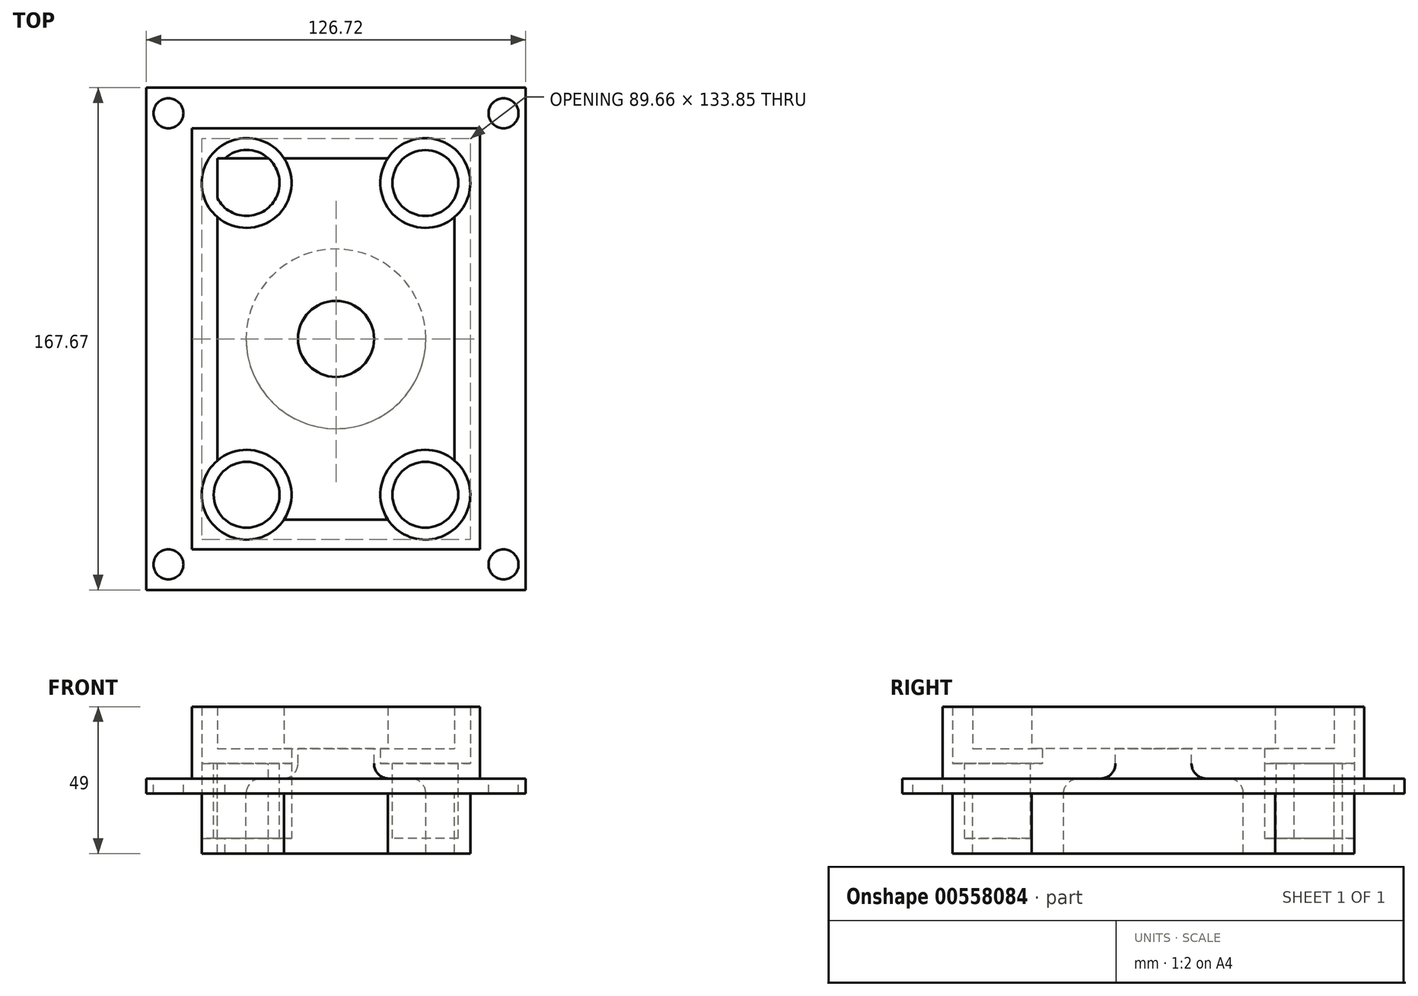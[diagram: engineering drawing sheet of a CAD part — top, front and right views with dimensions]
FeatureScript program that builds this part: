
annotation { "Feature Type Name" : "Feature", "Feature Type Description" : "" }
export const myFeature = defineFeature(function(context is Context, id is Id, definition is map)
    precondition{}
    {
        {
            var Q0;
            Q0=qCreatedBy(makeId("Top.planeOp"),FACE);
            var sketch = newSketch(context, id + "F0", { "sketchPlane" : qUnion([Q0])});
            skLineSegment(sketch, "E0.bottom", {"start": v(-50.77, 68.15) * mm, "end": v(45.43, 68.15) * mm});
            skLineSegment(sketch, "E0.top", {"start": v(-50.77, -72.5) * mm, "end": v(45.43, -72.5) * mm});
            skLineSegment(sketch, "E0.left", {"start": v(-50.77, 68.15) * mm, "end": v(-50.77, -72.5) * mm});
            skLineSegment(sketch, "E0.right", {"start": v(45.43, 68.15) * mm, "end": v(45.43, -72.5) * mm});
            skCircle(sketch, "E1", {"center": v(-2.67, -2.17) * mm, "radius": 12.7 * mm});
            skLineSegment(sketch, "E2.bottom", {"start": v(-42.27, 58.15) * mm, "end": v(36.93, 58.15) * mm});
            skLineSegment(sketch, "E2.top", {"start": v(-42.27, -62.5) * mm, "end": v(36.93, -62.5) * mm});
            skLineSegment(sketch, "E2.left", {"start": v(-42.27, 58.15) * mm, "end": v(-42.27, -62.5) * mm});
            skLineSegment(sketch, "E2.right", {"start": v(36.93, 58.15) * mm, "end": v(36.93, -62.5) * mm});
            skCircle(sketch, "E3", {"center": v(-32.5, 49.88) * mm, "radius": 15 * mm});
            skCircle(sketch, "E4", {"center": v(-32.5, -54.23) * mm, "radius": 15 * mm});
            skCircle(sketch, "E5", {"center": v(27.17, -54.23) * mm, "radius": 15 * mm});
            skLineSegment(sketch, "E6.bottom", {"start": v(-32.5, 49.88) * mm, "end": v(27.17, 49.88) * mm, "construction": true});
            skLineSegment(sketch, "E6.top", {"start": v(-32.5, -54.23) * mm, "end": v(27.17, -54.23) * mm, "construction": true});
            skLineSegment(sketch, "E6.left", {"start": v(-32.5, 49.88) * mm, "end": v(-32.5, -54.23) * mm, "construction": true});
            skLineSegment(sketch, "E6.right", {"start": v(27.17, 49.88) * mm, "end": v(27.17, -54.23) * mm, "construction": true});
            skCircle(sketch, "E7", {"center": v(27.17, 49.88) * mm, "radius": 15 * mm});
            skCircle(sketch, "E8", {"center": v(-32.5, 49.88) * mm, "radius": 11 * mm});
            skCircle(sketch, "E9", {"center": v(27.17, 49.88) * mm, "radius": 11 * mm});
            skCircle(sketch, "E10", {"center": v(27.17, -54.23) * mm, "radius": 11 * mm});
            skCircle(sketch, "E11", {"center": v(-32.5, -54.23) * mm, "radius": 11 * mm});
            skSolve(sketch);
        }
        {
            var Q0;
            Q0=makeQuery(id+"F0.imprint","IMPRINT",FACE,{"disambiguationData":[TD([[makeQuery(id+"F0.imprint","IMPRINT",EDGE,{"derivedFrom":sQuery(id+"F0.wireOp",EDGE,"E1")}),-1.0]])]});
            var Q1;
            Q1=makeQuery(id+"F0.imprint","IMPRINT",FACE,{"disambiguationData":[TD([[makeQuery(id+"F0.imprint","IMPRINT",EDGE,{"derivedFrom":sQuery(id+"F0.wireOp",EDGE,"E3")}),1.0]])]});
            var Q2;
            Q2=makeQuery(id+"F0.imprint","IMPRINT",FACE,{"disambiguationData":[TD([[makeQuery(id+"F0.imprint","IMPRINT",EDGE,{"derivedFrom":sQuery(id+"F0.wireOp",EDGE,"E7")}),1.0]])]});
            var Q3;
            Q3=makeQuery(id+"F0.imprint","IMPRINT",FACE,{"disambiguationData":[TD([[makeQuery(id+"F0.imprint","IMPRINT",EDGE,{"derivedFrom":sQuery(id+"F0.wireOp",EDGE,"E4")}),1.0]])]});
            var Q4;
            Q4=makeQuery(id+"F0.imprint","IMPRINT",FACE,{"disambiguationData":[TD([[makeQuery(id+"F0.imprint","IMPRINT",EDGE,{"derivedFrom":sQuery(id+"F0.wireOp",EDGE,"E0.bottom")}),-1.0]])]});
            var Q5;
            Q5=makeQuery(id+"F0.imprint","IMPRINT",FACE,{"disambiguationData":[TD([[makeQuery(id+"F0.imprint","IMPRINT",EDGE,{"derivedFrom":sQuery(id+"F0.wireOp",EDGE,"E5")}),1.0]])]});
            var Q6;
            {var subQ0=sQuery(id+"F0.wireOp",EDGE,"E2.left");var subQ1=sQuery(id+"F0.wireOp",EDGE,"E2.top");var subQ2=makeQuery(id+"F0.imprint","INTERSECT",VERTEX,{"derivedFrom":[subQ1,subQ0]});Q6=makeQuery(id+"F0.imprint","IMPRINT",FACE,{"disambiguationData":[TD([[makeQuery(id+"F0.imprint","IMPRINT",EDGE,{"disambiguationData":[TD([[subQ2,-1.0]])],"derivedFrom":subQ1}),-1.0]])]});}
            var Q7;
            {var subQ1=sQuery(id+"F0.wireOp",EDGE,"E2.top");var subQ5=sQuery(id+"F0.wireOp",EDGE,"E5");var subQ9=makeQuery(id+"F0.imprint","INTERSECT",VERTEX,{"derivedFrom":[subQ1,subQ5]});Q7=makeQuery(id+"F0.imprint","IMPRINT",FACE,{"disambiguationData":[TD([[makeQuery(id+"F0.imprint","IMPRINT",EDGE,{"disambiguationData":[TD([[subQ9,-1.0]])],"derivedFrom":subQ1}),-1.0]])]});}
            var Q8;
            {var subQ3=sQuery(id+"F0.wireOp",EDGE,"E7");var subQ5=sQuery(id+"F0.wireOp",EDGE,"E2.bottom");var subQ9=makeQuery(id+"F0.imprint","INTERSECT",VERTEX,{"derivedFrom":[subQ5,subQ3]});Q8=makeQuery(id+"F0.imprint","IMPRINT",FACE,{"disambiguationData":[TD([[makeQuery(id+"F0.imprint","IMPRINT",EDGE,{"disambiguationData":[TD([[subQ9,-1.0]])],"derivedFrom":subQ5}),1.0]])]});}
            var Q9;
            {var subQ0=sQuery(id+"F0.wireOp",EDGE,"E2.right");var subQ1=sQuery(id+"F0.wireOp",EDGE,"E2.bottom");var subQ2=makeQuery(id+"F0.imprint","INTERSECT",VERTEX,{"derivedFrom":[subQ1,subQ0]});Q9=makeQuery(id+"F0.imprint","IMPRINT",FACE,{"disambiguationData":[TD([[makeQuery(id+"F0.imprint","IMPRINT",EDGE,{"disambiguationData":[TD([[subQ2,1.0]])],"derivedFrom":subQ1}),-1.0]])]});}
            var Q10;
            {var subQ1=sQuery(id+"F0.wireOp",EDGE,"E2.left");var subQ6=sQuery(id+"F0.wireOp",EDGE,"E2.bottom");var subQ7=makeQuery(id+"F0.imprint","INTERSECT",VERTEX,{"derivedFrom":[subQ6,subQ1]});Q10=makeQuery(id+"F0.imprint","IMPRINT",FACE,{"disambiguationData":[TD([[makeQuery(id+"F0.imprint","IMPRINT",EDGE,{"disambiguationData":[TD([[subQ7,-1.0]])],"derivedFrom":subQ6}),1.0]])]});}
            var Q11;
            {var subQ0=sQuery(id+"F0.wireOp",EDGE,"E2.left");var subQ1=sQuery(id+"F0.wireOp",EDGE,"E2.bottom");var subQ2=makeQuery(id+"F0.imprint","INTERSECT",VERTEX,{"derivedFrom":[subQ1,subQ0]});Q11=makeQuery(id+"F0.imprint","IMPRINT",FACE,{"disambiguationData":[TD([[makeQuery(id+"F0.imprint","IMPRINT",EDGE,{"disambiguationData":[TD([[subQ2,-1.0]])],"derivedFrom":subQ1}),-1.0]])]});}
            var Q12;
            {var subQ0=sQuery(id+"F0.wireOp",EDGE,"E2.right");var subQ1=sQuery(id+"F0.wireOp",EDGE,"E2.top");var subQ2=makeQuery(id+"F0.imprint","INTERSECT",VERTEX,{"derivedFrom":[subQ1,subQ0]});Q12=makeQuery(id+"F0.imprint","IMPRINT",FACE,{"disambiguationData":[TD([[makeQuery(id+"F0.imprint","IMPRINT",EDGE,{"disambiguationData":[TD([[subQ2,1.0]])],"derivedFrom":subQ1}),1.0]])]});}
            var Q13;
            {var subQ0=sQuery(id+"F0.wireOp",EDGE,"E2.left");var subQ1=sQuery(id+"F0.wireOp",EDGE,"E2.top");var subQ2=makeQuery(id+"F0.imprint","INTERSECT",VERTEX,{"derivedFrom":[subQ1,subQ0]});Q13=makeQuery(id+"F0.imprint","IMPRINT",FACE,{"disambiguationData":[TD([[makeQuery(id+"F0.imprint","IMPRINT",EDGE,{"disambiguationData":[TD([[subQ2,-1.0]])],"derivedFrom":subQ1}),1.0]])]});}
            extrude(context, id + "F1", {"entities" : qUnion([Q0, Q1, Q2, Q3, Q4, Q5, Q6, Q7, Q8, Q9, Q10, Q11, Q12, Q13]), "oppositeDirection" : true, "depth" : 5 * mm, "offsetDistance" : 25 * mm});
        }
        {
            var Q0;
            Q0=makeQuery(id+"F0.imprint","IMPRINT",FACE,{"disambiguationData":[TD([[makeQuery(id+"F0.imprint","IMPRINT",EDGE,{"derivedFrom":sQuery(id+"F0.wireOp",EDGE,"E1")}),-1.0]])]});
            extrude(context, id + "F2", {"entities" : qUnion([Q0]), "operationType" : NewBodyOperationType.ADD, "depth" : 5 * mm, "offsetDistance" : 25 * mm});
        }
        {
            var Q0;
            Q0=makeQuery(id+"F0.imprint","IMPRINT",FACE,{"disambiguationData":[TD([[makeQuery(id+"F0.imprint","IMPRINT",EDGE,{"derivedFrom":sQuery(id+"F0.wireOp",EDGE,"E0.bottom")}),-1.0]])]});
            extrude(context, id + "F3", {"entities" : qUnion([Q0]), "operationType" : NewBodyOperationType.ADD, "depth" : 19 * mm, "offsetDistance" : 25 * mm});
        }
        {
            var Q0;
            Q0=makeQuery(id+"F1.opExtrude","CAP_FACE",FACE,{"disambiguationData":[OSD([sQuery(id+"F0.wireOp",EDGE,"E0.bottom"),sQuery(id+"F0.wireOp",EDGE,"E0.top"),sQuery(id+"F0.wireOp",EDGE,"E0.left"),sQuery(id+"F0.wireOp",EDGE,"E0.right"),sQuery(id+"F0.wireOp",EDGE,"E1")])],"isStart":false});
            var sketch = newSketch(context, id + "F4", { "sketchPlane" : qUnion([Q0])});
            skLineSegment(sketch, "E12.bottom", {"start": v(-66.03, 86.01) * mm, "end": v(60.7, 86.01) * mm});
            skLineSegment(sketch, "E12.top", {"start": v(-66.03, -81.66) * mm, "end": v(60.7, -81.66) * mm});
            skLineSegment(sketch, "E12.left", {"start": v(-66.03, 86.01) * mm, "end": v(-66.03, -81.66) * mm});
            skLineSegment(sketch, "E12.right", {"start": v(60.7, 86.01) * mm, "end": v(60.7, -81.66) * mm});
            skPoint(sketch, "E12.middle", {"position": v(-2.67, 2.17) * mm});
            skLineSegment(sketch, "E13.bottom", {"start": v(-58.6, 77.5) * mm, "end": v(53.27, 77.5) * mm, "construction": true});
            skLineSegment(sketch, "E13.top", {"start": v(-58.6, -73.15) * mm, "end": v(53.27, -73.15) * mm, "construction": true});
            skLineSegment(sketch, "E13.left", {"start": v(-58.6, 77.5) * mm, "end": v(-58.6, -73.15) * mm, "construction": true});
            skLineSegment(sketch, "E13.right", {"start": v(53.27, 77.5) * mm, "end": v(53.27, -73.15) * mm, "construction": true});
            skCircle(sketch, "E14", {"center": v(-58.6, 77.5) * mm, "radius": 5 * mm});
            skCircle(sketch, "E15", {"center": v(53.27, 77.5) * mm, "radius": 5 * mm});
            skCircle(sketch, "E16", {"center": v(53.27, -73.15) * mm, "radius": 5 * mm});
            skCircle(sketch, "E17", {"center": v(-58.6, -73.15) * mm, "radius": 5 * mm});
            skCircle(sketch, "E18", {"center": v(-2.67, 2.17) * mm, "radius": 30 * mm});
            skSolve(sketch);
        }
        {
            var Q0;
            Q0=makeQuery(id+"F4.imprint","IMPRINT",FACE,{"disambiguationData":[TD([[makeQuery(id+"F4.imprint","IMPRINT",EDGE,{"derivedFrom":sQuery(id+"F4.wireOp",EDGE,"E12.bottom")}),-1.0]])]});
            var Q1;
            Q1=makeQuery(id+"F4.imprint","IMPRINT",FACE,{"disambiguationData":[TD([[makeQuery(id+"F4.imprint","IMPRINT",EDGE,{"derivedFrom":makeQuery(id+"F1.opExtrude","CAP_EDGE",EDGE,{"disambiguationData":[OSD([sQuery(id+"F0.wireOp",EDGE,"E0.bottom")])],"isStart":false})}),1.0]])]});
            var Q2;
            Q2=makeQuery(id+"F2.opExtrude","CAP_FACE",FACE,{"disambiguationData":[OSD([sQuery(id+"F0.wireOp",EDGE,"E1"),sQuery(id+"F0.wireOp",EDGE,"E2.bottom"),sQuery(id+"F0.wireOp",EDGE,"E2.top"),sQuery(id+"F0.wireOp",EDGE,"E2.left"),sQuery(id+"F0.wireOp",EDGE,"E2.right"),sQuery(id+"F0.wireOp",EDGE,"E3"),sQuery(id+"F0.wireOp",EDGE,"E4"),sQuery(id+"F0.wireOp",EDGE,"E5"),sQuery(id+"F0.wireOp",EDGE,"E7")])],"isStart":false});
            var Q3;
            Q3=makeQuery(id+"F4.imprint","IMPRINT",FACE,{"disambiguationData":[TD([[makeQuery(id+"F4.imprint","IMPRINT",EDGE,{"derivedFrom":makeQuery(id+"F1.opExtrude","CAP_EDGE",EDGE,{"disambiguationData":[OSD([sQuery(id+"F0.wireOp",EDGE,"E10")])],"isStart":false})}),-1.0]])]});
            var Q4;
            Q4=makeQuery(id+"F4.imprint","IMPRINT",FACE,{"disambiguationData":[TD([[makeQuery(id+"F4.imprint","IMPRINT",EDGE,{"derivedFrom":makeQuery(id+"F1.opExtrude","CAP_EDGE",EDGE,{"disambiguationData":[OSD([sQuery(id+"F0.wireOp",EDGE,"E11")])],"isStart":false})}),-1.0]])]});
            var Q5;
            Q5=makeQuery(id+"F4.imprint","IMPRINT",FACE,{"disambiguationData":[TD([[makeQuery(id+"F4.imprint","IMPRINT",EDGE,{"derivedFrom":makeQuery(id+"F1.opExtrude","CAP_EDGE",EDGE,{"disambiguationData":[OSD([sQuery(id+"F0.wireOp",EDGE,"E8")])],"isStart":false})}),-1.0]])]});
            var Q6;
            Q6=makeQuery(id+"F4.imprint","IMPRINT",FACE,{"disambiguationData":[TD([[makeQuery(id+"F4.imprint","IMPRINT",EDGE,{"derivedFrom":makeQuery(id+"F1.opExtrude","CAP_EDGE",EDGE,{"disambiguationData":[OSD([sQuery(id+"F0.wireOp",EDGE,"E9")])],"isStart":false})}),-1.0]])]});
            extrude(context, id + "F5", {"entities" : qUnion([Q0, Q1, Q2, Q3, Q4, Q5, Q6]), "operationType" : NewBodyOperationType.ADD, "depth" : 5 * mm, "offsetDistance" : 25 * mm});
        }
        {
            var Q0;
            {var subQ1=sQuery(id+"F0.wireOp",EDGE,"E2.left");var subQ6=sQuery(id+"F0.wireOp",EDGE,"E2.bottom");var subQ7=makeQuery(id+"F0.imprint","INTERSECT",VERTEX,{"derivedFrom":[subQ6,subQ1]});Q0=makeQuery(id+"F0.imprint","IMPRINT",FACE,{"disambiguationData":[TD([[makeQuery(id+"F0.imprint","IMPRINT",EDGE,{"disambiguationData":[TD([[subQ7,-1.0]])],"derivedFrom":subQ6}),1.0]])]});}
            var Q1;
            {var subQ0=sQuery(id+"F0.wireOp",EDGE,"E8");var subQ1=sQuery(id+"F0.wireOp",EDGE,"E2.bottom");var subQ2=makeQuery(id+"F0.imprint","INTERSECT",VERTEX,{"disambiguationData":[OD(0.0)],"derivedFrom":[subQ1,subQ0]});Q1=makeQuery(id+"F0.imprint","IMPRINT",FACE,{"disambiguationData":[TD([[makeQuery(id+"F0.imprint","IMPRINT",EDGE,{"disambiguationData":[TD([[subQ2,-1.0]])],"derivedFrom":subQ1}),1.0]])]});}
            var Q2;
            {var subQ0=sQuery(id+"F0.wireOp",EDGE,"E2.left");var subQ1=sQuery(id+"F0.wireOp",EDGE,"E2.bottom");var subQ2=makeQuery(id+"F0.imprint","INTERSECT",VERTEX,{"derivedFrom":[subQ1,subQ0]});Q2=makeQuery(id+"F0.imprint","IMPRINT",FACE,{"disambiguationData":[TD([[makeQuery(id+"F0.imprint","IMPRINT",EDGE,{"disambiguationData":[TD([[subQ2,-1.0]])],"derivedFrom":subQ1}),-1.0]])]});}
            var Q3;
            {var subQ0=sQuery(id+"F0.wireOp",EDGE,"E8");var subQ1=sQuery(id+"F0.wireOp",EDGE,"E2.left");var subQ2=makeQuery(id+"F0.imprint","INTERSECT",VERTEX,{"disambiguationData":[OD(0.0)],"derivedFrom":[subQ1,subQ0]});Q3=makeQuery(id+"F0.imprint","IMPRINT",FACE,{"disambiguationData":[TD([[makeQuery(id+"F0.imprint","IMPRINT",EDGE,{"disambiguationData":[TD([[subQ2,-1.0]])],"derivedFrom":subQ1}),-1.0]])]});}
            var Q4;
            {var subQ0=sQuery(id+"F0.wireOp",EDGE,"E8");var subQ1=sQuery(id+"F0.wireOp",EDGE,"E2.bottom");var subQ2=makeQuery(id+"F0.imprint","INTERSECT",VERTEX,{"disambiguationData":[OD(1.0)],"derivedFrom":[subQ1,subQ0]});Q4=makeQuery(id+"F0.imprint","IMPRINT",FACE,{"disambiguationData":[TD([[makeQuery(id+"F0.imprint","IMPRINT",EDGE,{"disambiguationData":[TD([[subQ2,-1.0]])],"derivedFrom":subQ1}),-1.0]])]});}
            var Q5;
            {var subQ0=sQuery(id+"F0.wireOp",EDGE,"E8");var subQ1=sQuery(id+"F0.wireOp",EDGE,"E2.bottom");var subQ2=makeQuery(id+"F0.imprint","INTERSECT",VERTEX,{"disambiguationData":[OD(0.0)],"derivedFrom":[subQ1,subQ0]});Q5=makeQuery(id+"F0.imprint","IMPRINT",FACE,{"disambiguationData":[TD([[makeQuery(id+"F0.imprint","IMPRINT",EDGE,{"disambiguationData":[TD([[subQ2,-1.0]])],"derivedFrom":subQ1}),-1.0]])]});}
            var Q6;
            {var subQ3=sQuery(id+"F0.wireOp",EDGE,"E7");var subQ5=sQuery(id+"F0.wireOp",EDGE,"E2.bottom");var subQ9=makeQuery(id+"F0.imprint","INTERSECT",VERTEX,{"derivedFrom":[subQ5,subQ3]});Q6=makeQuery(id+"F0.imprint","IMPRINT",FACE,{"disambiguationData":[TD([[makeQuery(id+"F0.imprint","IMPRINT",EDGE,{"disambiguationData":[TD([[subQ9,-1.0]])],"derivedFrom":subQ5}),1.0]])]});}
            var Q7;
            {var subQ0=sQuery(id+"F0.wireOp",EDGE,"E9");var subQ1=sQuery(id+"F0.wireOp",EDGE,"E2.right");var subQ2=makeQuery(id+"F0.imprint","INTERSECT",VERTEX,{"disambiguationData":[OD(0.0)],"derivedFrom":[subQ1,subQ0]});Q7=makeQuery(id+"F0.imprint","IMPRINT",FACE,{"disambiguationData":[TD([[makeQuery(id+"F0.imprint","IMPRINT",EDGE,{"disambiguationData":[TD([[subQ2,-1.0]])],"derivedFrom":subQ1}),1.0]])]});}
            var Q8;
            {var subQ0=sQuery(id+"F0.wireOp",EDGE,"E9");var subQ1=sQuery(id+"F0.wireOp",EDGE,"E2.bottom");var subQ2=makeQuery(id+"F0.imprint","INTERSECT",VERTEX,{"disambiguationData":[OD(0.0)],"derivedFrom":[subQ1,subQ0]});Q8=makeQuery(id+"F0.imprint","IMPRINT",FACE,{"disambiguationData":[TD([[makeQuery(id+"F0.imprint","IMPRINT",EDGE,{"disambiguationData":[TD([[subQ2,-1.0]])],"derivedFrom":subQ1}),-1.0]])]});}
            var Q9;
            {var subQ0=sQuery(id+"F0.wireOp",EDGE,"E2.right");var subQ1=sQuery(id+"F0.wireOp",EDGE,"E2.bottom");var subQ2=makeQuery(id+"F0.imprint","INTERSECT",VERTEX,{"derivedFrom":[subQ1,subQ0]});Q9=makeQuery(id+"F0.imprint","IMPRINT",FACE,{"disambiguationData":[TD([[makeQuery(id+"F0.imprint","IMPRINT",EDGE,{"disambiguationData":[TD([[subQ2,1.0]])],"derivedFrom":subQ1}),-1.0]])]});}
            var Q10;
            {var subQ0=sQuery(id+"F0.wireOp",EDGE,"E9");var subQ1=sQuery(id+"F0.wireOp",EDGE,"E2.bottom");var subQ2=makeQuery(id+"F0.imprint","INTERSECT",VERTEX,{"disambiguationData":[OD(0.0)],"derivedFrom":[subQ1,subQ0]});Q10=makeQuery(id+"F0.imprint","IMPRINT",FACE,{"disambiguationData":[TD([[makeQuery(id+"F0.imprint","IMPRINT",EDGE,{"disambiguationData":[TD([[subQ2,-1.0]])],"derivedFrom":subQ1}),1.0]])]});}
            var Q11;
            {var subQ0=sQuery(id+"F0.wireOp",EDGE,"E7");var subQ1=sQuery(id+"F0.wireOp",EDGE,"E2.bottom");var subQ2=makeQuery(id+"F0.imprint","INTERSECT",VERTEX,{"derivedFrom":[subQ1,subQ0]});Q11=makeQuery(id+"F0.imprint","IMPRINT",FACE,{"disambiguationData":[TD([[makeQuery(id+"F0.imprint","IMPRINT",EDGE,{"disambiguationData":[TD([[subQ2,-1.0]])],"derivedFrom":subQ1}),-1.0]])]});}
            var Q12;
            {var subQ1=sQuery(id+"F0.wireOp",EDGE,"E2.top");var subQ5=sQuery(id+"F0.wireOp",EDGE,"E5");var subQ9=makeQuery(id+"F0.imprint","INTERSECT",VERTEX,{"derivedFrom":[subQ1,subQ5]});Q12=makeQuery(id+"F0.imprint","IMPRINT",FACE,{"disambiguationData":[TD([[makeQuery(id+"F0.imprint","IMPRINT",EDGE,{"disambiguationData":[TD([[subQ9,-1.0]])],"derivedFrom":subQ1}),-1.0]])]});}
            var Q13;
            {var subQ0=sQuery(id+"F0.wireOp",EDGE,"E5");var subQ1=sQuery(id+"F0.wireOp",EDGE,"E2.top");var subQ2=makeQuery(id+"F0.imprint","INTERSECT",VERTEX,{"derivedFrom":[subQ1,subQ0]});Q13=makeQuery(id+"F0.imprint","IMPRINT",FACE,{"disambiguationData":[TD([[makeQuery(id+"F0.imprint","IMPRINT",EDGE,{"disambiguationData":[TD([[subQ2,-1.0]])],"derivedFrom":subQ1}),1.0]])]});}
            var Q14;
            {var subQ0=sQuery(id+"F0.wireOp",EDGE,"E10");var subQ1=sQuery(id+"F0.wireOp",EDGE,"E2.top");var subQ2=makeQuery(id+"F0.imprint","INTERSECT",VERTEX,{"disambiguationData":[OD(0.0)],"derivedFrom":[subQ1,subQ0]});Q14=makeQuery(id+"F0.imprint","IMPRINT",FACE,{"disambiguationData":[TD([[makeQuery(id+"F0.imprint","IMPRINT",EDGE,{"disambiguationData":[TD([[subQ2,-1.0]])],"derivedFrom":subQ1}),1.0]])]});}
            var Q15;
            {var subQ0=sQuery(id+"F0.wireOp",EDGE,"E10");var subQ1=sQuery(id+"F0.wireOp",EDGE,"E2.top");var subQ2=makeQuery(id+"F0.imprint","INTERSECT",VERTEX,{"disambiguationData":[OD(0.0)],"derivedFrom":[subQ1,subQ0]});Q15=makeQuery(id+"F0.imprint","IMPRINT",FACE,{"disambiguationData":[TD([[makeQuery(id+"F0.imprint","IMPRINT",EDGE,{"disambiguationData":[TD([[subQ2,-1.0]])],"derivedFrom":subQ1}),-1.0]])]});}
            var Q16;
            {var subQ0=sQuery(id+"F0.wireOp",EDGE,"E10");var subQ1=sQuery(id+"F0.wireOp",EDGE,"E2.right");var subQ2=makeQuery(id+"F0.imprint","INTERSECT",VERTEX,{"disambiguationData":[OD(0.0)],"derivedFrom":[subQ1,subQ0]});Q16=makeQuery(id+"F0.imprint","IMPRINT",FACE,{"disambiguationData":[TD([[makeQuery(id+"F0.imprint","IMPRINT",EDGE,{"disambiguationData":[TD([[subQ2,-1.0]])],"derivedFrom":subQ1}),1.0]])]});}
            var Q17;
            {var subQ0=sQuery(id+"F0.wireOp",EDGE,"E2.right");var subQ1=sQuery(id+"F0.wireOp",EDGE,"E2.top");var subQ2=makeQuery(id+"F0.imprint","INTERSECT",VERTEX,{"derivedFrom":[subQ1,subQ0]});Q17=makeQuery(id+"F0.imprint","IMPRINT",FACE,{"disambiguationData":[TD([[makeQuery(id+"F0.imprint","IMPRINT",EDGE,{"disambiguationData":[TD([[subQ2,1.0]])],"derivedFrom":subQ1}),1.0]])]});}
            var Q18;
            {var subQ0=sQuery(id+"F0.wireOp",EDGE,"E2.left");var subQ1=sQuery(id+"F0.wireOp",EDGE,"E2.top");var subQ2=makeQuery(id+"F0.imprint","INTERSECT",VERTEX,{"derivedFrom":[subQ1,subQ0]});Q18=makeQuery(id+"F0.imprint","IMPRINT",FACE,{"disambiguationData":[TD([[makeQuery(id+"F0.imprint","IMPRINT",EDGE,{"disambiguationData":[TD([[subQ2,-1.0]])],"derivedFrom":subQ1}),-1.0]])]});}
            var Q19;
            {var subQ0=sQuery(id+"F0.wireOp",EDGE,"E11");var subQ1=sQuery(id+"F0.wireOp",EDGE,"E2.top");var subQ2=makeQuery(id+"F0.imprint","INTERSECT",VERTEX,{"disambiguationData":[OD(1.0)],"derivedFrom":[subQ1,subQ0]});Q19=makeQuery(id+"F0.imprint","IMPRINT",FACE,{"disambiguationData":[TD([[makeQuery(id+"F0.imprint","IMPRINT",EDGE,{"disambiguationData":[TD([[subQ2,-1.0]])],"derivedFrom":subQ1}),1.0]])]});}
            var Q20;
            {var subQ0=sQuery(id+"F0.wireOp",EDGE,"E11");var subQ1=sQuery(id+"F0.wireOp",EDGE,"E2.top");var subQ2=makeQuery(id+"F0.imprint","INTERSECT",VERTEX,{"disambiguationData":[OD(0.0)],"derivedFrom":[subQ1,subQ0]});Q20=makeQuery(id+"F0.imprint","IMPRINT",FACE,{"disambiguationData":[TD([[makeQuery(id+"F0.imprint","IMPRINT",EDGE,{"disambiguationData":[TD([[subQ2,-1.0]])],"derivedFrom":subQ1}),1.0]])]});}
            var Q21;
            {var subQ0=sQuery(id+"F0.wireOp",EDGE,"E11");var subQ1=sQuery(id+"F0.wireOp",EDGE,"E2.left");var subQ2=makeQuery(id+"F0.imprint","INTERSECT",VERTEX,{"disambiguationData":[OD(0.0)],"derivedFrom":[subQ1,subQ0]});Q21=makeQuery(id+"F0.imprint","IMPRINT",FACE,{"disambiguationData":[TD([[makeQuery(id+"F0.imprint","IMPRINT",EDGE,{"disambiguationData":[TD([[subQ2,-1.0]])],"derivedFrom":subQ1}),-1.0]])]});}
            var Q22;
            {var subQ0=sQuery(id+"F0.wireOp",EDGE,"E2.left");var subQ1=sQuery(id+"F0.wireOp",EDGE,"E2.top");var subQ2=makeQuery(id+"F0.imprint","INTERSECT",VERTEX,{"derivedFrom":[subQ1,subQ0]});Q22=makeQuery(id+"F0.imprint","IMPRINT",FACE,{"disambiguationData":[TD([[makeQuery(id+"F0.imprint","IMPRINT",EDGE,{"disambiguationData":[TD([[subQ2,-1.0]])],"derivedFrom":subQ1}),1.0]])]});}
            var Q23;
            {var subQ0=sQuery(id+"F0.wireOp",EDGE,"E11");var subQ1=sQuery(id+"F0.wireOp",EDGE,"E2.top");var subQ2=makeQuery(id+"F0.imprint","INTERSECT",VERTEX,{"disambiguationData":[OD(0.0)],"derivedFrom":[subQ1,subQ0]});Q23=makeQuery(id+"F0.imprint","IMPRINT",FACE,{"disambiguationData":[TD([[makeQuery(id+"F0.imprint","IMPRINT",EDGE,{"disambiguationData":[TD([[subQ2,-1.0]])],"derivedFrom":subQ1}),-1.0]])]});}
            var Q24;
            Q24=makeQuery(id+"F0.imprint","IMPRINT",FACE,{"disambiguationData":[TD([[makeQuery(id+"F0.imprint","IMPRINT",EDGE,{"derivedFrom":sQuery(id+"F0.wireOp",EDGE,"E1")}),-1.0]])]});
            var Q25;
            Q25=makeQuery(id+"F0.imprint","IMPRINT",FACE,{"disambiguationData":[TD([[makeQuery(id+"F0.imprint","IMPRINT",EDGE,{"derivedFrom":sQuery(id+"F0.wireOp",EDGE,"E1")}),1.0]])]});
            extrude(context, id + "F6", {"entities" : qUnion([Q0, Q1, Q2, Q3, Q4, Q5, Q6, Q7, Q8, Q9, Q10, Q11, Q12, Q13, Q14, Q15, Q16, Q17, Q18, Q19, Q20, Q21, Q22, Q23, Q24, Q25]), "operationType" : NewBodyOperationType.ADD, "oppositeDirection" : true, "depth" : 30 * mm, "offsetDistance" : 25 * mm});
        }
        {
            var Q0;
            {var subQ0=sQuery(id+"F0.wireOp",EDGE,"E9");var subQ1=sQuery(id+"F0.wireOp",EDGE,"E2.bottom");var subQ2=makeQuery(id+"F0.imprint","INTERSECT",VERTEX,{"disambiguationData":[OD(0.0)],"derivedFrom":[subQ1,subQ0]});Q0=makeQuery(id+"F0.imprint","IMPRINT",FACE,{"disambiguationData":[TD([[makeQuery(id+"F0.imprint","IMPRINT",EDGE,{"disambiguationData":[TD([[subQ2,-1.0]])],"derivedFrom":subQ1}),-1.0]])]});}
            var Q1;
            {var subQ0=sQuery(id+"F0.wireOp",EDGE,"E9");var subQ1=sQuery(id+"F0.wireOp",EDGE,"E2.bottom");var subQ2=makeQuery(id+"F0.imprint","INTERSECT",VERTEX,{"disambiguationData":[OD(0.0)],"derivedFrom":[subQ1,subQ0]});Q1=makeQuery(id+"F0.imprint","IMPRINT",FACE,{"disambiguationData":[TD([[makeQuery(id+"F0.imprint","IMPRINT",EDGE,{"disambiguationData":[TD([[subQ2,-1.0]])],"derivedFrom":subQ1}),1.0]])]});}
            var Q2;
            {var subQ0=sQuery(id+"F0.wireOp",EDGE,"E9");var subQ1=sQuery(id+"F0.wireOp",EDGE,"E2.right");var subQ2=makeQuery(id+"F0.imprint","INTERSECT",VERTEX,{"disambiguationData":[OD(0.0)],"derivedFrom":[subQ1,subQ0]});Q2=makeQuery(id+"F0.imprint","IMPRINT",FACE,{"disambiguationData":[TD([[makeQuery(id+"F0.imprint","IMPRINT",EDGE,{"disambiguationData":[TD([[subQ2,-1.0]])],"derivedFrom":subQ1}),1.0]])]});}
            var Q3;
            {var subQ0=sQuery(id+"F0.wireOp",EDGE,"E8");var subQ1=sQuery(id+"F0.wireOp",EDGE,"E2.bottom");var subQ2=makeQuery(id+"F0.imprint","INTERSECT",VERTEX,{"disambiguationData":[OD(0.0)],"derivedFrom":[subQ1,subQ0]});Q3=makeQuery(id+"F0.imprint","IMPRINT",FACE,{"disambiguationData":[TD([[makeQuery(id+"F0.imprint","IMPRINT",EDGE,{"disambiguationData":[TD([[subQ2,-1.0]])],"derivedFrom":subQ1}),-1.0]])]});}
            var Q4;
            {var subQ0=sQuery(id+"F0.wireOp",EDGE,"E8");var subQ1=sQuery(id+"F0.wireOp",EDGE,"E2.bottom");var subQ2=makeQuery(id+"F0.imprint","INTERSECT",VERTEX,{"disambiguationData":[OD(0.0)],"derivedFrom":[subQ1,subQ0]});Q4=makeQuery(id+"F0.imprint","IMPRINT",FACE,{"disambiguationData":[TD([[makeQuery(id+"F0.imprint","IMPRINT",EDGE,{"disambiguationData":[TD([[subQ2,-1.0]])],"derivedFrom":subQ1}),1.0]])]});}
            var Q5;
            {var subQ0=sQuery(id+"F0.wireOp",EDGE,"E8");var subQ1=sQuery(id+"F0.wireOp",EDGE,"E2.left");var subQ2=makeQuery(id+"F0.imprint","INTERSECT",VERTEX,{"disambiguationData":[OD(0.0)],"derivedFrom":[subQ1,subQ0]});Q5=makeQuery(id+"F0.imprint","IMPRINT",FACE,{"disambiguationData":[TD([[makeQuery(id+"F0.imprint","IMPRINT",EDGE,{"disambiguationData":[TD([[subQ2,-1.0]])],"derivedFrom":subQ1}),-1.0]])]});}
            var Q6;
            {var subQ0=sQuery(id+"F0.wireOp",EDGE,"E10");var subQ1=sQuery(id+"F0.wireOp",EDGE,"E2.top");var subQ2=makeQuery(id+"F0.imprint","INTERSECT",VERTEX,{"disambiguationData":[OD(0.0)],"derivedFrom":[subQ1,subQ0]});Q6=makeQuery(id+"F0.imprint","IMPRINT",FACE,{"disambiguationData":[TD([[makeQuery(id+"F0.imprint","IMPRINT",EDGE,{"disambiguationData":[TD([[subQ2,-1.0]])],"derivedFrom":subQ1}),1.0]])]});}
            var Q7;
            {var subQ0=sQuery(id+"F0.wireOp",EDGE,"E10");var subQ1=sQuery(id+"F0.wireOp",EDGE,"E2.right");var subQ2=makeQuery(id+"F0.imprint","INTERSECT",VERTEX,{"disambiguationData":[OD(0.0)],"derivedFrom":[subQ1,subQ0]});Q7=makeQuery(id+"F0.imprint","IMPRINT",FACE,{"disambiguationData":[TD([[makeQuery(id+"F0.imprint","IMPRINT",EDGE,{"disambiguationData":[TD([[subQ2,-1.0]])],"derivedFrom":subQ1}),1.0]])]});}
            var Q8;
            {var subQ0=sQuery(id+"F0.wireOp",EDGE,"E10");var subQ1=sQuery(id+"F0.wireOp",EDGE,"E2.top");var subQ2=makeQuery(id+"F0.imprint","INTERSECT",VERTEX,{"disambiguationData":[OD(0.0)],"derivedFrom":[subQ1,subQ0]});Q8=makeQuery(id+"F0.imprint","IMPRINT",FACE,{"disambiguationData":[TD([[makeQuery(id+"F0.imprint","IMPRINT",EDGE,{"disambiguationData":[TD([[subQ2,-1.0]])],"derivedFrom":subQ1}),-1.0]])]});}
            var Q9;
            {var subQ0=sQuery(id+"F0.wireOp",EDGE,"E11");var subQ1=sQuery(id+"F0.wireOp",EDGE,"E2.top");var subQ2=makeQuery(id+"F0.imprint","INTERSECT",VERTEX,{"disambiguationData":[OD(0.0)],"derivedFrom":[subQ1,subQ0]});Q9=makeQuery(id+"F0.imprint","IMPRINT",FACE,{"disambiguationData":[TD([[makeQuery(id+"F0.imprint","IMPRINT",EDGE,{"disambiguationData":[TD([[subQ2,-1.0]])],"derivedFrom":subQ1}),1.0]])]});}
            var Q10;
            {var subQ0=sQuery(id+"F0.wireOp",EDGE,"E11");var subQ1=sQuery(id+"F0.wireOp",EDGE,"E2.left");var subQ2=makeQuery(id+"F0.imprint","INTERSECT",VERTEX,{"disambiguationData":[OD(0.0)],"derivedFrom":[subQ1,subQ0]});Q10=makeQuery(id+"F0.imprint","IMPRINT",FACE,{"disambiguationData":[TD([[makeQuery(id+"F0.imprint","IMPRINT",EDGE,{"disambiguationData":[TD([[subQ2,-1.0]])],"derivedFrom":subQ1}),-1.0]])]});}
            var Q11;
            {var subQ0=sQuery(id+"F0.wireOp",EDGE,"E11");var subQ1=sQuery(id+"F0.wireOp",EDGE,"E2.top");var subQ2=makeQuery(id+"F0.imprint","INTERSECT",VERTEX,{"disambiguationData":[OD(0.0)],"derivedFrom":[subQ1,subQ0]});Q11=makeQuery(id+"F0.imprint","IMPRINT",FACE,{"disambiguationData":[TD([[makeQuery(id+"F0.imprint","IMPRINT",EDGE,{"disambiguationData":[TD([[subQ2,-1.0]])],"derivedFrom":subQ1}),-1.0]])]});}
            extrude(context, id + "F7", {"entities" : qUnion([Q0, Q1, Q2, Q3, Q4, Q5, Q6, Q7, Q8, Q9, Q10, Q11]), "operationType" : NewBodyOperationType.REMOVE, "oppositeDirection" : true, "depth" : 25 * mm, "offsetDistance" : 25 * mm});
        }
        {
            var Q0;
            Q0=makeQuery(id+"F6.boolean.opBoolean","SPLIT",FACE,{"derivedFrom":makeQuery(id+"F6.opExtrude","CAP_FACE",FACE,{"disambiguationData":[OSD([sQuery(id+"F0.wireOp",EDGE,"E2.bottom"),sQuery(id+"F0.wireOp",EDGE,"E2.top"),sQuery(id+"F0.wireOp",EDGE,"E2.left"),sQuery(id+"F0.wireOp",EDGE,"E2.right"),sQuery(id+"F0.wireOp",EDGE,"E3"),sQuery(id+"F0.wireOp",EDGE,"E4"),sQuery(id+"F0.wireOp",EDGE,"E5"),sQuery(id+"F0.wireOp",EDGE,"E7")])],"isStart":true})});
            var sketch = newSketch(context, id + "F8", { "sketchPlane" : qUnion([Q0])});
            skSolve(sketch);
        }
        {
            var Q0;
            {var subQ0=sQuery(id+"F0.wireOp",EDGE,"E1");Q0=makeQuery(id+"F8.imprint","IMPRINT",FACE,{"disambiguationData":[TD([[makeQuery(id+"F8.imprint","IMPRINT",EDGE,{"derivedFrom":makeQuery(id+"F6.boolean.opBoolean","INTERSECT",EDGE,{"derivedFrom":[makeQuery(id+"F2.boolean.opBoolean","MERGE",FACE,{"derivedFrom":[makeQuery(id+"F1.opExtrude","SWEPT_FACE",FACE,{"disambiguationData":[OSD([subQ0])]}),makeQuery(id+"F2.opExtrude","SWEPT_FACE",FACE,{"disambiguationData":[OSD([subQ0])]})]}),makeQuery(id+"F6.opExtrude","CAP_FACE",FACE,{"disambiguationData":[OSD([sQuery(id+"F0.wireOp",EDGE,"E2.bottom"),sQuery(id+"F0.wireOp",EDGE,"E2.top"),sQuery(id+"F0.wireOp",EDGE,"E2.left"),sQuery(id+"F0.wireOp",EDGE,"E2.right"),sQuery(id+"F0.wireOp",EDGE,"E3"),sQuery(id+"F0.wireOp",EDGE,"E4"),sQuery(id+"F0.wireOp",EDGE,"E5"),sQuery(id+"F0.wireOp",EDGE,"E7")])],"isStart":true})]})}),-1.0]])]});}
            extrude(context, id + "F9", {"entities" : qUnion([Q0]), "operationType" : NewBodyOperationType.REMOVE, "oppositeDirection" : true, "depth" : 35 * mm, "offsetDistance" : 25 * mm});
        }
        {
            var Q0;
            Q0=makeQuery(id+"F4.imprint","IMPRINT",FACE,{"disambiguationData":[TD([[makeQuery(id+"F4.imprint","IMPRINT",EDGE,{"derivedFrom":sQuery(id+"F4.wireOp",EDGE,"E18")}),1.0]])]});
            extrude(context, id + "F10", {"entities" : qUnion([Q0]), "operationType" : NewBodyOperationType.REMOVE, "depth" : 35 * mm, "offsetDistance" : 25 * mm});
        }
        {
            var Q0;
            Q0=makeQuery(id+"F10.boolean.opBoolean","COPY",FACE,{"derivedFrom":makeQuery(id+"F10.opExtrude","CAP_FACE",FACE,{"disambiguationData":[OSD([sQuery(id+"F0.wireOp",EDGE,"E1"),sQuery(id+"F4.wireOp",EDGE,"E18")])],"isStart":true})});
            fillet(context, id + "F11", {"entities" : qUnion([Q0]), "radius" : 5 * mm, "tangentPropagation" : true, "allowEdgeOverflow" : false});
        }
    });
